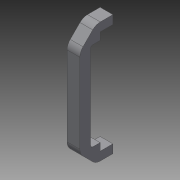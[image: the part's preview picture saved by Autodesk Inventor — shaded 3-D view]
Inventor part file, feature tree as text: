
AUTODESK INVENTOR PART (.ipt)
format: ipt  version: 2015 (Build 190159000, 159)  size: 105,984 bytes
history: native  units: in
note: dims shown in document units (in); Inventor stores cm internally (conversion verified against a paired STEP export)
features: extrude x1, fillet x1, sketch x1
ambient origin geometry x8: Origin, YZ Plane, XZ Plane, XY Plane, X Axis, Y Axis, Z Axis, Center Point
bodies: Solid1 (feature_tree)
feature tree (3):
  extrude  "Extrusion1"  Depth=0.2362in TaperAngle=0.0deg
  fillet  "Fillet1"  Radius=0.3937in
  sketch  "Sketch1"  dims[d4=1.9094in d10=0.2362in d11=0.0in d21=0.3937in d22=0.3937in d31=0.1969in d34=0.1969in d37=0.1575in d46=0.1378in d48=0.0394in d50=0.315in d51=0.1772in d52=0.2362in]
